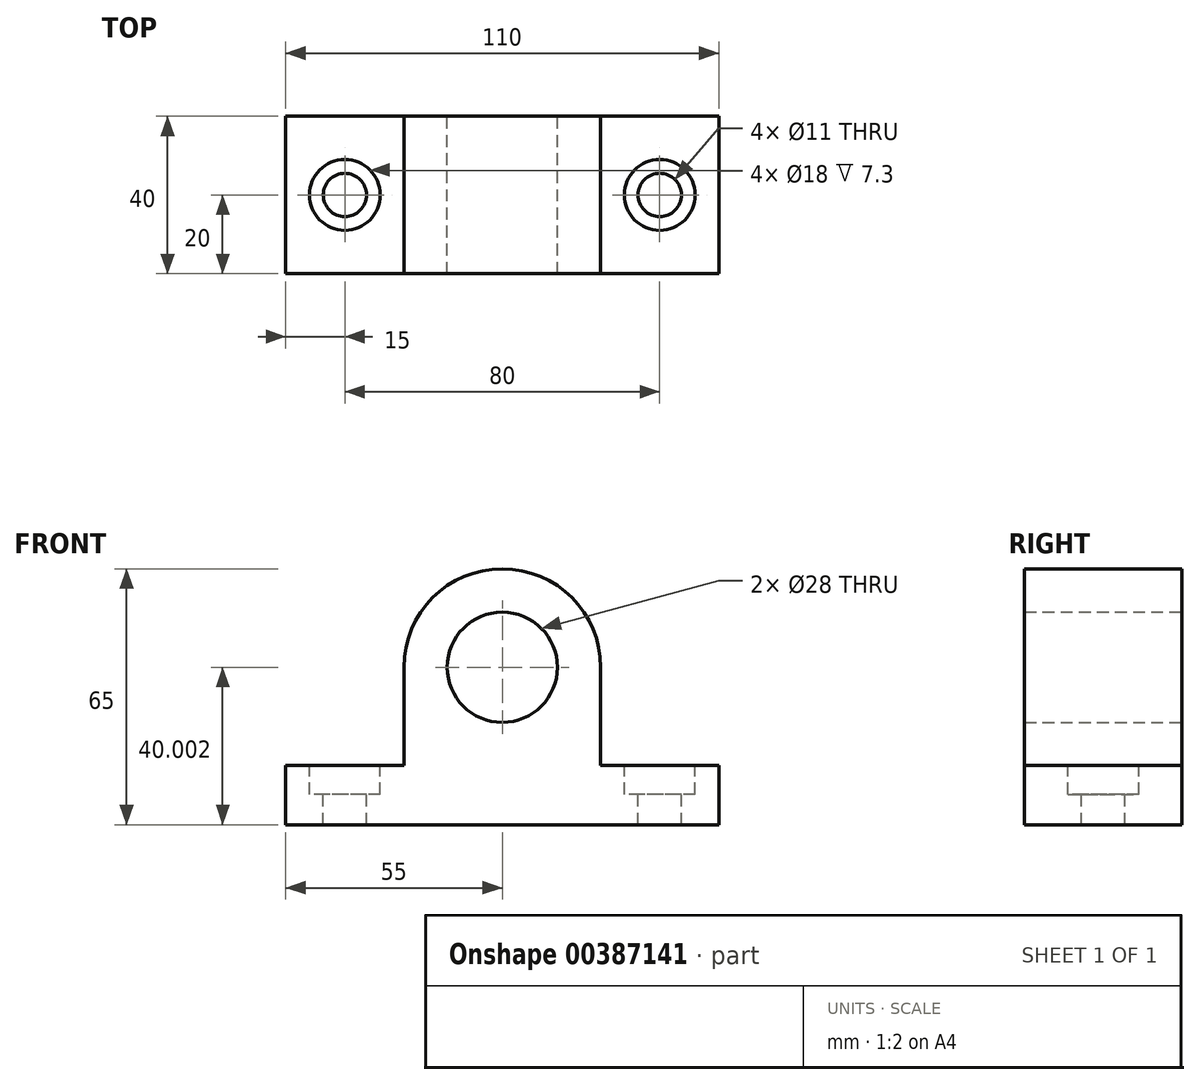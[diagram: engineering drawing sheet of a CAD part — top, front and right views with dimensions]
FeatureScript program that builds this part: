
annotation { "Feature Type Name" : "Feature", "Feature Type Description" : "" }
export const myFeature = defineFeature(function(context is Context, id is Id, definition is map)
    precondition{}
    {
        {
            var Q0;
            Q0=qCreatedBy(makeId("Front.planeOp"),FACE);
            var sketch = newSketch(context, id + "F0", { "sketchPlane" : qUnion([Q0])});
            skLineSegment(sketch, "E0.top", {"start": v(-55, -21.77) * mm, "end": v(55, -21.77) * mm});
            skLineSegment(sketch, "E0.left", {"start": v(-55, -6.77) * mm, "end": v(-55, -21.77) * mm});
            skLineSegment(sketch, "E1.top", {"start": v(-55, -6.77) * mm, "end": v(-25, -6.77) * mm});
            skLineSegment(sketch, "E1.right", {"start": v(-25, 18.23) * mm, "end": v(-25, -6.77) * mm});
            skLineSegment(sketch, "E2.top", {"start": v(55, -6.77) * mm, "end": v(25, -6.77) * mm});
            skLineSegment(sketch, "E2.right", {"start": v(25, 18.23) * mm, "end": v(25, -6.77) * mm});
            skArc(sketch, "E3", {"start": v(25, 18.23) * mm, "mid": v(0, 43.23) * mm, "end": v(-25, 18.23) * mm});
            skLineSegment(sketch, "E4", {"start": v(55, -6.77) * mm, "end": v(55, -21.77) * mm});
            skCircle(sketch, "E5", {"center": v(0, 18.23) * mm, "radius": 14 * mm});
            skSolve(sketch);
        }
        {
            var Q0;
            Q0=makeQuery(id+"F0.imprint","IMPRINT",FACE,{"disambiguationData":[TD([[makeQuery(id+"F0.imprint","IMPRINT",EDGE,{"derivedFrom":sQuery(id+"F0.wireOp",EDGE,"E0.top")}),1.0]])]});
            extrude(context, id + "F1", {"entities" : qUnion([Q0]), "depth" : 40 * mm});
        }
        {
            var Q0;
            Q0=makeQuery(id+"F1.opExtrude","SWEPT_FACE",FACE,{"disambiguationData":[OSD([sQuery(id+"F0.wireOp",EDGE,"E1.top")])]});
            var sketch = newSketch(context, id + "F2", { "sketchPlane" : qUnion([Q0])});
            skCircle(sketch, "E6", {"center": v(-40, -20) * mm, "radius": 5.5 * mm});
            skCircle(sketch, "E7", {"center": v(-40, -20) * mm, "radius": 9 * mm});
            skCircle(sketch, "E8", {"center": v(40, -20) * mm, "radius": 5.5 * mm});
            skCircle(sketch, "E9", {"center": v(40, -20) * mm, "radius": 9 * mm});
            skSolve(sketch);
        }
        {
            var Q0;
            Q0=makeQuery(id+"F2.imprint","IMPRINT",FACE,{"disambiguationData":[TD([[makeQuery(id+"F2.imprint","IMPRINT",EDGE,{"derivedFrom":sQuery(id+"F2.wireOp",EDGE,"E8")}),1.0]])]});
            var Q1;
            Q1=makeQuery(id+"F2.imprint","IMPRINT",FACE,{"disambiguationData":[TD([[makeQuery(id+"F2.imprint","IMPRINT",EDGE,{"derivedFrom":sQuery(id+"F2.wireOp",EDGE,"E6")}),1.0]])]});
            extrude(context, id + "F3", {"entities" : qUnion([Q0, Q1]), "operationType" : NewBodyOperationType.REMOVE, "oppositeDirection" : true, "depth" : 25 * mm});
        }
        {
            var Q0;
            Q0=makeQuery(id+"F2.imprint","IMPRINT",FACE,{"disambiguationData":[TD([[makeQuery(id+"F2.imprint","IMPRINT",EDGE,{"derivedFrom":sQuery(id+"F2.wireOp",EDGE,"E6")}),-1.0]])]});
            var Q1;
            Q1=makeQuery(id+"F2.imprint","IMPRINT",FACE,{"disambiguationData":[TD([[makeQuery(id+"F2.imprint","IMPRINT",EDGE,{"derivedFrom":sQuery(id+"F2.wireOp",EDGE,"E8")}),-1.0]])]});
            extrude(context, id + "F4", {"entities" : qUnion([Q0, Q1]), "operationType" : NewBodyOperationType.REMOVE, "oppositeDirection" : true, "depth" : 7.3 * mm});
        }
    });
